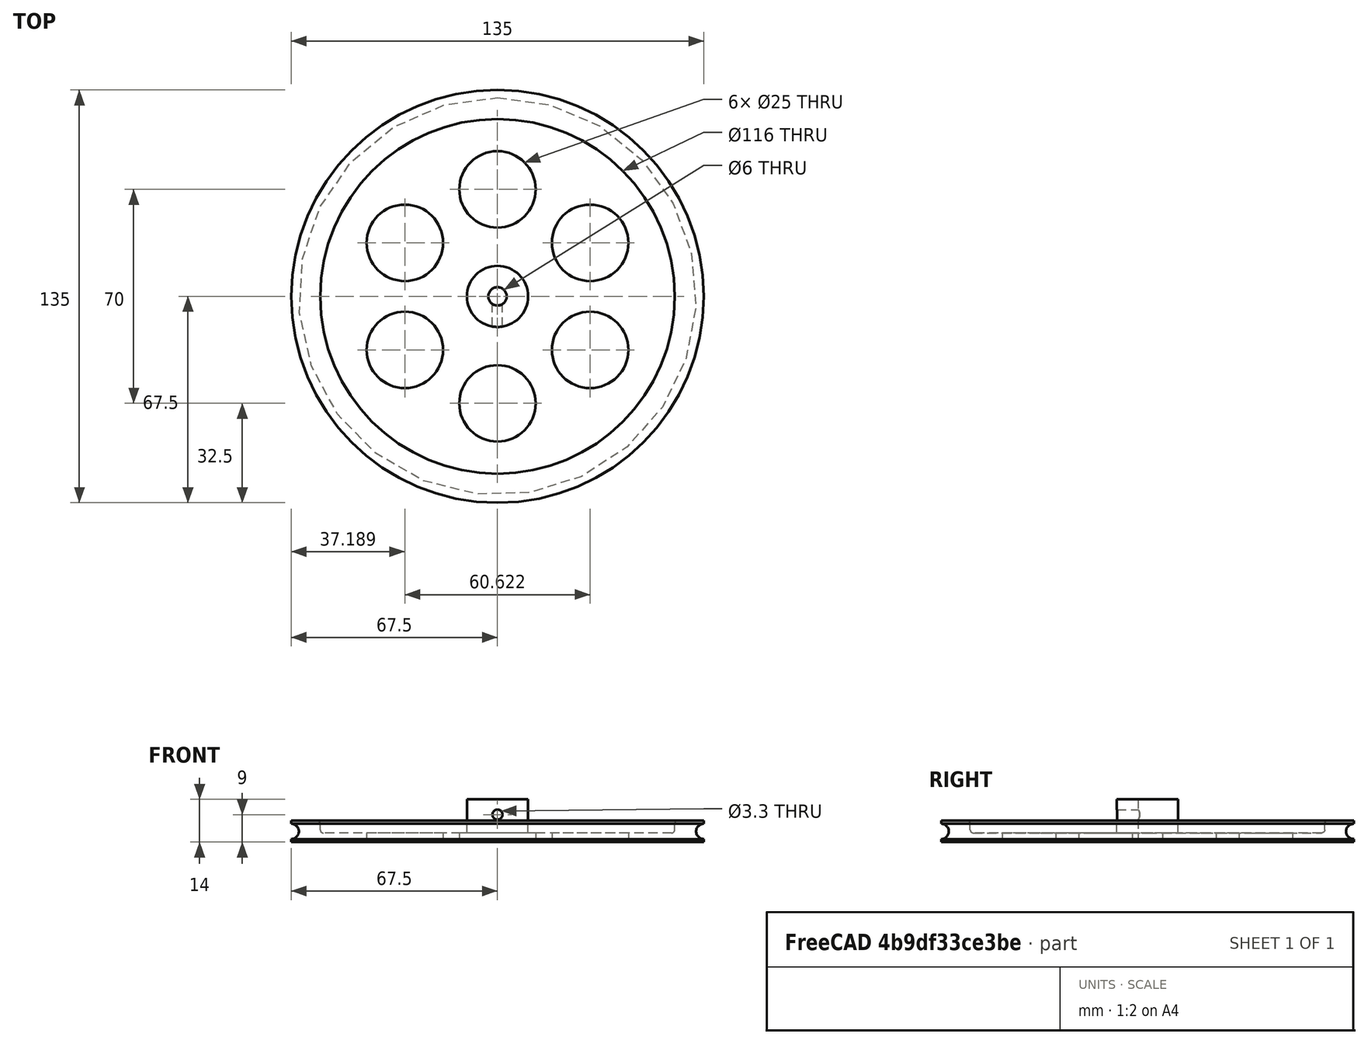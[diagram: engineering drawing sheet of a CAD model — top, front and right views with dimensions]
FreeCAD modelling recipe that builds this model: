
FCSTD DOCUMENT  (FreeCAD 0.17R13522 (Git))
Label: Rad
License: All rights reserved
LicenseURL: http://en.wikipedia.org/wiki/All_rights_reserved
objects: TechDraw::DrawViewDimension×17, Sketcher::SketchObject×4, Part::Cylinder×3, PartDesign::Hole×3, TechDraw::DrawViewAnnotation×3, TechDraw::DrawSVGTemplate×2, PartDesign::Fillet×2, TechDraw::DrawProjGroupItem×2, TechDraw::DrawProjGroup×2, TechDraw::DrawPage×2, Part::Cut×1, Part::Fuse×1, PartDesign::FeatureBase×1, PartDesign::Groove×1, PartDesign::Body×1, TechDraw::DrawViewSection×1, TechDraw::DrawViewPart×1
note: 21 computed .brp shape members not serialized (recipe doc carries the construction recipe); baked Part::Feature solids carry a one-line shape summary decoded from their .brp

FEATURE [Part::Cylinder] Cylinder  label="Zylinder"
  Angle = 360
  AttacherType = Attacher::AttachEngine3D
  Height = 7
  Radius = 67.5
FEATURE [Part::Cylinder] Cylinder001  label="Zylinder001"
  Angle = 360
  AttacherType = Attacher::AttachEngine3D
  Height = 4
  Placement = pos=(0,0,3) rot=(0,0,1;0rad)
  Radius = 58
FEATURE [Part::Cut] Cut
  Base = -> Cylinder
  Tool = -> Cylinder001
FEATURE [Part::Cylinder] Cylinder002  label="Zylinder002"
  Angle = 360
  AttacherType = Attacher::AttachEngine3D
  Height = 14
  Radius = 10
FEATURE [Part::Fuse] Fusion
  Base = -> Cut
  Tool = -> Cylinder002
FEATURE [PartDesign::FeatureBase] BaseFeature
  BaseFeature = -> Fusion
FEATURE [Sketcher::SketchObject] Sketch
  MapMode = 5
  Placement = pos=(0,0,14) rot=(0,0,1;0rad)
  Support = -> [BaseFeature]
  sketch-geometry (1):
    g0: Circle CenterX=0 CenterY=0 CenterZ=0 NormalX=0 NormalY=0 NormalZ=1 AngleXU=0 Radius=3
  constraints (2):
    c: Coincident(g0,g-1)
    c: Radius(g0) = 3
FEATURE [PartDesign::Hole] Hole
  BaseFeature = -> BaseFeature
  Depth = 25
  DepthType = 1
  Diameter = 6
  DrillPoint = 1
  DrillPointAngle = 118
  HoleCutCountersinkAngle = 90
  HoleCutDepth = 0
  HoleCutDiameter = 0
  HoleCutType = 0
  ModelActualThread = false
  Profile = -> Sketch
  Tapered = false
  TaperedAngle = 90
  ThreadAngle = 0
  ThreadClass = 0
  ThreadCutOffInner = 0
  ThreadCutOffOuter = 0
  ThreadDirection = 0
  ThreadFit = 0
  ThreadPitch = 0
  ThreadSize = 0
  ThreadType = 0
  Threaded = false
FEATURE [Sketcher::SketchObject] Sketch001
  MapMode = 5
  Placement = pos=(0,0,0) rot=(0.57735,0.57735,0.57735;2.0944rad)
  Support = -> [YZ_Plane]
  sketch-geometry (1):
    g0: Circle CenterX=67.5 CenterY=3.5 CenterZ=0 NormalX=0 NormalY=0 NormalZ=1 AngleXU=0 Radius=2.5
  constraints (3):
    c: Radius(g0) = 2.5
    c: DistanceX(g-1,g0) = 67.5
    c: DistanceY(g-1,g0) = 3.5
FEATURE [PartDesign::Groove] Groove
  Angle = 360
  Axis = (0,0,1)
  Base = (0,0,0)
  BaseFeature = -> Hole
  Profile = -> Sketch001
  ReferenceAxis = -> Sketch001 [V_Axis]
FEATURE [Sketcher::SketchObject] Sketch002
  MapMode = 5
  Placement = pos=(0,0,3) rot=(0,0,1;0rad)
  Support = -> [Groove]
  sketch-geometry (6):
    g0: Circle CenterX=0 CenterY=35 CenterZ=0 NormalX=0 NormalY=0 NormalZ=1 AngleXU=0 Radius=12.5
    g1: Circle CenterX=30.3109 CenterY=17.5 CenterZ=0 NormalX=0 NormalY=0 NormalZ=1 AngleXU=0 Radius=12.5
    g2: Circle CenterX=30.3109 CenterY=-17.5 CenterZ=0 NormalX=0 NormalY=0 NormalZ=1 AngleXU=0 Radius=12.5
    g3: Circle CenterX=-30.3109 CenterY=-17.5 CenterZ=0 NormalX=0 NormalY=0 NormalZ=1 AngleXU=0 Radius=12.5
    g4: Circle CenterX=0 CenterY=-35 CenterZ=0 NormalX=0 NormalY=0 NormalZ=1 AngleXU=0 Radius=12.5
    g5: Circle CenterX=-30.3109 CenterY=17.5 CenterZ=0 NormalX=0 NormalY=0 NormalZ=1 AngleXU=0 Radius=12.5
  constraints (18):
    c: Radius(g0) = 12.5
    c: Radius(g1) = 12.5
    c: Radius(g2) = 12.5
    c: Radius(g3) = 12.5
    c: Radius(g4) = 12.5
    c: Radius(g5) = 12.5
    c: Distance(g3,g5) = 35
    c: Distance(g3,g4) = 35
    c: Distance(g4,g2) = 35
    c: Distance(g1,g2) = 35
    c: Distance(g0,g1) = 35
    c: Distance(g0,g5) = 35
    c: Vertical(g-1,g0)
    c: Vertical(g0,g4)
    c: DistanceY(g-1,g0) = 35
    c: Distance(g-1,g3) = 35
    c: Distance(g-1,g2) = 35
    c: Distance(g-1,g4) = 35
FEATURE [PartDesign::Hole] Hole001
  BaseFeature = -> Groove
  Depth = 25
  DepthType = 1
  Diameter = 25
  DrillPoint = 1
  DrillPointAngle = 118
  HoleCutCountersinkAngle = 90
  HoleCutDepth = 0
  HoleCutDiameter = 0
  HoleCutType = 0
  ModelActualThread = false
  Profile = -> Sketch002
  Tapered = false
  TaperedAngle = 90
  ThreadAngle = 0
  ThreadClass = 0
  ThreadCutOffInner = 0
  ThreadCutOffOuter = 0
  ThreadDirection = 0
  ThreadFit = 0
  ThreadPitch = 0
  ThreadSize = 0
  ThreadType = 0
  Threaded = false
FEATURE [Sketcher::SketchObject] Sketch003
  AttachmentOffset = pos=(0,0,10) rot=(0,0,1;0rad)
  MapMode = 5
  Placement = pos=(0,-10,-1e-12) rot=(1,0,0;1.5708rad)
  Support = -> [XZ_Plane]
  sketch-geometry (1):
    g0: Circle CenterX=0 CenterY=9 CenterZ=0 NormalX=0 NormalY=0 NormalZ=1 AngleXU=0 Radius=1
  constraints (3):
    c: PointOnObject(g0,g-2)
    c: DistanceY(g-1,g0) = 9
    c: Radius(g0) = 1
FEATURE [PartDesign::Hole] Hole002
  BaseFeature = -> Hole001
  Depth = 10
  DepthType = 0
  Diameter = 3.3
  DrillPoint = 1
  DrillPointAngle = 118
  HoleCutCountersinkAngle = 90
  HoleCutDepth = 0
  HoleCutDiameter = 4
  HoleCutType = 0
  ModelActualThread = false
  Profile = -> Sketch003
  Tapered = false
  TaperedAngle = 90
  ThreadAngle = 60
  ThreadClass = 0
  ThreadCutOffInner = 0.0757772
  ThreadCutOffOuter = 0.151554
  ThreadDirection = 1
  ThreadFit = 0
  ThreadPitch = 0.7
  ThreadSize = 5
  ThreadType = 1
  Threaded = true
FEATURE [TechDraw::DrawSVGTemplate] Template
  EditableTexts = Designed_by_Name=Christian Dengler; FC-Date=25.05.2018; FC-SC=1/2; FC-SH=1/2; FC-Title=Wheel; Subtitle=Outer dimensions
  Height = 210
  Orientation = 1
  Width = 297
FEATURE [TechDraw::DrawSVGTemplate] Template001
  EditableTexts = Designed_by_Name=Christian Dengler; FC-Date=25.05.2018; FC-SC=3/2; FC-SH=2/2; FC-Title=Wheel; Subtitle=Vertikal Dimensions
  Height = 210
  Orientation = 1
  Width = 297
FEATURE [PartDesign::Fillet] Fillet
  Base = -> Hole002 [Edge21]
  BaseFeature = -> Hole002
  Radius = 1
FEATURE [PartDesign::Fillet] Fillet001
  Base = -> Fillet [Edge3]
  BaseFeature = -> Fillet
  Radius = 1
FEATURE [PartDesign::Body] Body
  BaseFeature = -> Fusion
  Group = -> [BaseFeature,Sketch,Hole,Sketch001,Groove,Sketch002,Hole001,Sketch003,Hole002,Fillet,Fillet001]
  Origin = -> Origin
  Tip = -> Fillet001
FEATURE [TechDraw::DrawProjGroupItem] ProjItem  label="Front"
  CoarseView = false
  Direction = (0,0,1)
  Focus = 100
  HardHidden = false
  IsoCount = 0
  IsoHidden = false
  IsoVisible = false
  LockPosition = false
  Perspective = false
  Rotation = 0
  RotationVector = (0,-1,0)
  ScaleType = 0
  SeamHidden = false
  SeamVisible = false
  SmoothHidden = false
  SmoothVisible = false
  Source = -> [Body]
  Type = 0
  X = 83.4265
  Y = 84.9155
FEATURE [TechDraw::DrawProjGroup] ProjGroup
  Anchor = -> ProjItem
  AutoDistribute = true
  CubeDirs = (6) [(1,-3.06162e-16,-1.22465e-16),(1.22465e-16,6.12323e-17,1),(-3.06162e-16,-1,6.12323e-17),(-1.22465e-16,-6.12323e-17,-1),(3.06162e-16,1,-6.12323e-17),(-1,3.06162e-16,1.22465e-16)]
  CubeRotations = (6) [(3.06162e-16,-1,6.12323e-17),(3.06162e-16,-1,6.12323e-17),(-1.22465e-16,1.83697e-16,1),(-3.06162e-16,1,-6.12323e-17),(1.22465e-16,-1.83697e-16,-1),(3.06162e-16,-1,6.12323e-17)]
  LockPosition = false
  ProjectionType = 0
  Rotation = 0
  Scale = 0.8
  ScaleType = 2
  Source = -> [Body]
  Views = -> [ProjItem]
  X = 84.2325
  Y = 145.33
  spacingX = 15
  spacingY = 15
FEATURE [TechDraw::DrawViewDimension] Dimension001
  FormatSpec = %.2f
  LockPosition = false
  MeasureType = 1
  References2D = -> [ProjItem]
  Rotation = 0
  ScaleType = 0
  Type = 5
  X = 100.355
  Y = 6.81886
FEATURE [TechDraw::DrawProjGroupItem] ProjItem001  label="Front001"
  CoarseView = false
  Direction = (0,-1,0)
  Focus = 100
  HardHidden = false
  IsoCount = 0
  IsoHidden = false
  IsoVisible = false
  LockPosition = false
  Perspective = false
  Rotation = 0
  RotationVector = (1,0,0)
  ScaleType = 0
  SeamHidden = false
  SeamVisible = false
  SmoothHidden = false
  SmoothVisible = false
  Source = -> [Body]
  Type = 0
  X = 0
  Y = 0
FEATURE [TechDraw::DrawProjGroup] ProjGroup001
  Anchor = -> ProjItem001
  AutoDistribute = true
  CubeDirs = (6) [(0,-2.44929e-16,-1),(0,-1,2.44929e-16),(-1,0,0),(0,1,-2.44929e-16),(1,0,0),(0,2.44929e-16,1)]
  CubeRotations = (6) [(1,0,0),(1,0,0),(0,1,2.44929e-16),(-1,0,0),(0,-1,-2.44929e-16),(1,0,0)]
  LockPosition = false
  ProjectionType = 0
  Rotation = 0
  Scale = 1.5
  ScaleType = 2
  Source = -> [Body]
  Views = -> [ProjItem001]
  X = 125.507
  Y = 165.106
  spacingX = 15
  spacingY = 15
FEATURE [TechDraw::DrawViewSection] Section  label="Section A - A"
  BaseView = -> ProjItem001
  CoarseView = false
  Direction = (1,0,0)
  Focus = 100
  HardHidden = false
  HatchScale = 1
  IsoCount = 0
  IsoHidden = false
  IsoVisible = true
  LockPosition = true
  NameGeomPattern = Diamond
  Perspective = false
  Rotation = 0
  Scale = 1.5
  ScaleType = 2
  SeamHidden = false
  SeamVisible = false
  SectionDirection = 1
  SectionNormal = (1,0,0)
  SectionOrigin = (0,0,5)
  SectionSymbol = A
  SmoothHidden = true
  SmoothVisible = true
  Source = -> [Body]
  X = 122.714
  Y = 102.298
FEATURE [TechDraw::DrawViewDimension] Dimension010
  FormatSpec = %.2f
  LockPosition = false
  MeasureType = 1
  References2D = -> [Section]
  Rotation = 0
  ScaleType = 0
  Type = 2
  X = 132.997
  Y = -30.1162
FEATURE [TechDraw::DrawViewDimension] Dimension012
  FormatSpec = %.2f
  LockPosition = false
  MeasureType = 1
  References2D = -> [Section]
  Rotation = 0
  ScaleType = 0
  Type = 2
  X = 108.439
  Y = -30.488
FEATURE [TechDraw::DrawViewDimension] Dimension013
  FormatSpec = %.2f
  LockPosition = false
  MeasureType = 1
  References2D = -> [Section]
  Rotation = 0
  ScaleType = 0
  Type = 2
  X = 120.931
  Y = -29.5757
FEATURE [TechDraw::DrawViewDimension] Dimension014
  FormatSpec = %.2f
  LockPosition = false
  MeasureType = 1
  References2D = -> [Section]
  Rotation = 0
  ScaleType = 0
  Type = 5
  X = 55.1517
  Y = -27.6564
FEATURE [TechDraw::DrawViewPart] View
  CoarseView = false
  Direction = (1,-4,3)
  Focus = 100
  HardHidden = false
  IsoCount = 0
  IsoHidden = false
  IsoVisible = false
  LockPosition = false
  Perspective = false
  Rotation = 0
  Scale = 0.2
  ScaleType = 2
  SeamHidden = false
  SeamVisible = false
  SmoothHidden = false
  SmoothVisible = false
  Source = -> [Body]
  X = 238.198
  Y = 48.5539
FEATURE [TechDraw::DrawViewDimension] Dimension019
  FormatSpec = %.2f
  LockPosition = false
  MeasureType = 1
  References2D = -> [ProjItem]
  Rotation = 0
  ScaleType = 0
  Type = 5
  X = 93.6068
  Y = 45.7981
FEATURE [TechDraw::DrawViewDimension] Dimension
  FormatSpec = %.2f
  LockPosition = false
  MeasureType = 1
  References2D = -> [ProjItem]
  Rotation = 0
  ScaleType = 0
  Type = 0
  X = -62.2629
  Y = 19.4744
FEATURE [TechDraw::DrawViewDimension] Dimension020
  FormatSpec = %.2f
  LockPosition = false
  MeasureType = 1
  References2D = -> [ProjItem]
  Rotation = 0
  ScaleType = 0
  Type = 5
  X = 95.512
  Y = -47.9259
FEATURE [TechDraw::DrawViewDimension] Dimension021
  FormatSpec = %.2f
  LockPosition = false
  MeasureType = 1
  References2D = -> [ProjItem]
  Rotation = 0
  ScaleType = 0
  Type = 5
  X = 98.0046
  Y = -37.6723
FEATURE [TechDraw::DrawViewDimension] Dimension022
  FormatSpec = %.2f
  LockPosition = false
  MeasureType = 1
  References2D = -> [ProjItem]
  Rotation = 0
  ScaleType = 0
  Type = 5
  X = 95.394
  Y = 33.064
FEATURE [TechDraw::DrawViewDimension] Dimension023
  FormatSpec = %.2f
  LockPosition = false
  MeasureType = 1
  References2D = -> [ProjItem]
  Rotation = 0
  ScaleType = 0
  Type = 5
  X = 86.2344
  Y = 44.681
FEATURE [TechDraw::DrawViewAnnotation] Annotation
  Font = osifont
  LineSpace = 80
  LockPosition = false
  MaxWidth = 50
  Rotation = 0
  ScaleType = 0
  Text = Große Bohrungen: gleichmäßiges Hexagon auf Kreis mit Radius ca 35mm
  TextSize = 5
  TextStyle = 0
  X = 249.926
  Y = 144.99
FEATURE [TechDraw::DrawPage] Page
  KeepUpdated = true
  ProjectionType = 0
  Template = -> Template
  Views = -> [ProjGroup,Dimension001,View,Dimension019,Dimension,Dimension020,Dimension021,Dimension022,Dimension023,Annotation]
FEATURE [TechDraw::DrawViewDimension] Dimension024
  FormatSpec = %.2f
  LockPosition = false
  MeasureType = 1
  References2D = -> [Section]
  Rotation = 0
  ScaleType = 0
  Type = 2
  X = 146.33
  Y = 0
FEATURE [TechDraw::DrawViewDimension] Dimension025
  FormatSpec = %.2f
  LockPosition = false
  MeasureType = 1
  References2D = -> [Section]
  Rotation = 0
  ScaleType = 0
  Type = 4
  X = 69.4046
  Y = -35.1119
FEATURE [TechDraw::DrawViewDimension] Dimension026
  FormatSpec = %.2f
  LockPosition = false
  MeasureType = 1
  References2D = -> [Section]
  Rotation = 0
  ScaleType = 0
  Type = 2
  X = -48.0321
  Y = 20.8512
FEATURE [TechDraw::DrawViewDimension] Dimension027
  FormatSpec = %.2f
  LockPosition = false
  MeasureType = 1
  References2D = -> [Section]
  Rotation = 0
  ScaleType = 0
  Type = 2
  X = -64.9737
  Y = 21.9682
FEATURE [TechDraw::DrawViewAnnotation] Annotation001
  Font = osifont
  LineSpace = 80
  LockPosition = false
  MaxWidth = -1
  Rotation = 90
  ScaleType = 0
  Text = (eig. M4 Gewind)
  TextSize = 3
  TextStyle = 0
  X = 80.5848
  Y = 125.33
FEATURE [TechDraw::DrawViewAnnotation] Annotation002
  Font = osifont
  LineSpace = 80
  LockPosition = false
  MaxWidth = -1
  Rotation = 0
  ScaleType = 0
  Text = (Rundungen optional)
  TextSize = 3
  TextStyle = 0
  X = 42.819
  Y = 61.5518
FEATURE [TechDraw::DrawViewDimension] Dimension028
  FormatSpec = %.2f
  LockPosition = false
  MeasureType = 1
  References2D = -> [Section]
  Rotation = 0
  ScaleType = 0
  Type = 4
  X = -74.4632
  Y = -29.1875
FEATURE [TechDraw::DrawViewDimension] Dimension029
  FormatSpec = %.2f
  LockPosition = false
  MeasureType = 1
  References2D = -> [Section]
  Rotation = 0
  ScaleType = 0
  Type = 4
  X = -82.3548
  Y = -34.9071
FEATURE [TechDraw::DrawPage] Page001
  KeepUpdated = true
  ProjectionType = 0
  Template = -> Template001
  Views = -> [ProjGroup001,Section,Dimension010,Dimension012,Dimension013,Dimension014,Dimension024,Dimension025,Dimension026,Dimension027,Annotation001,Annotation002,Dimension028,Dimension029]
